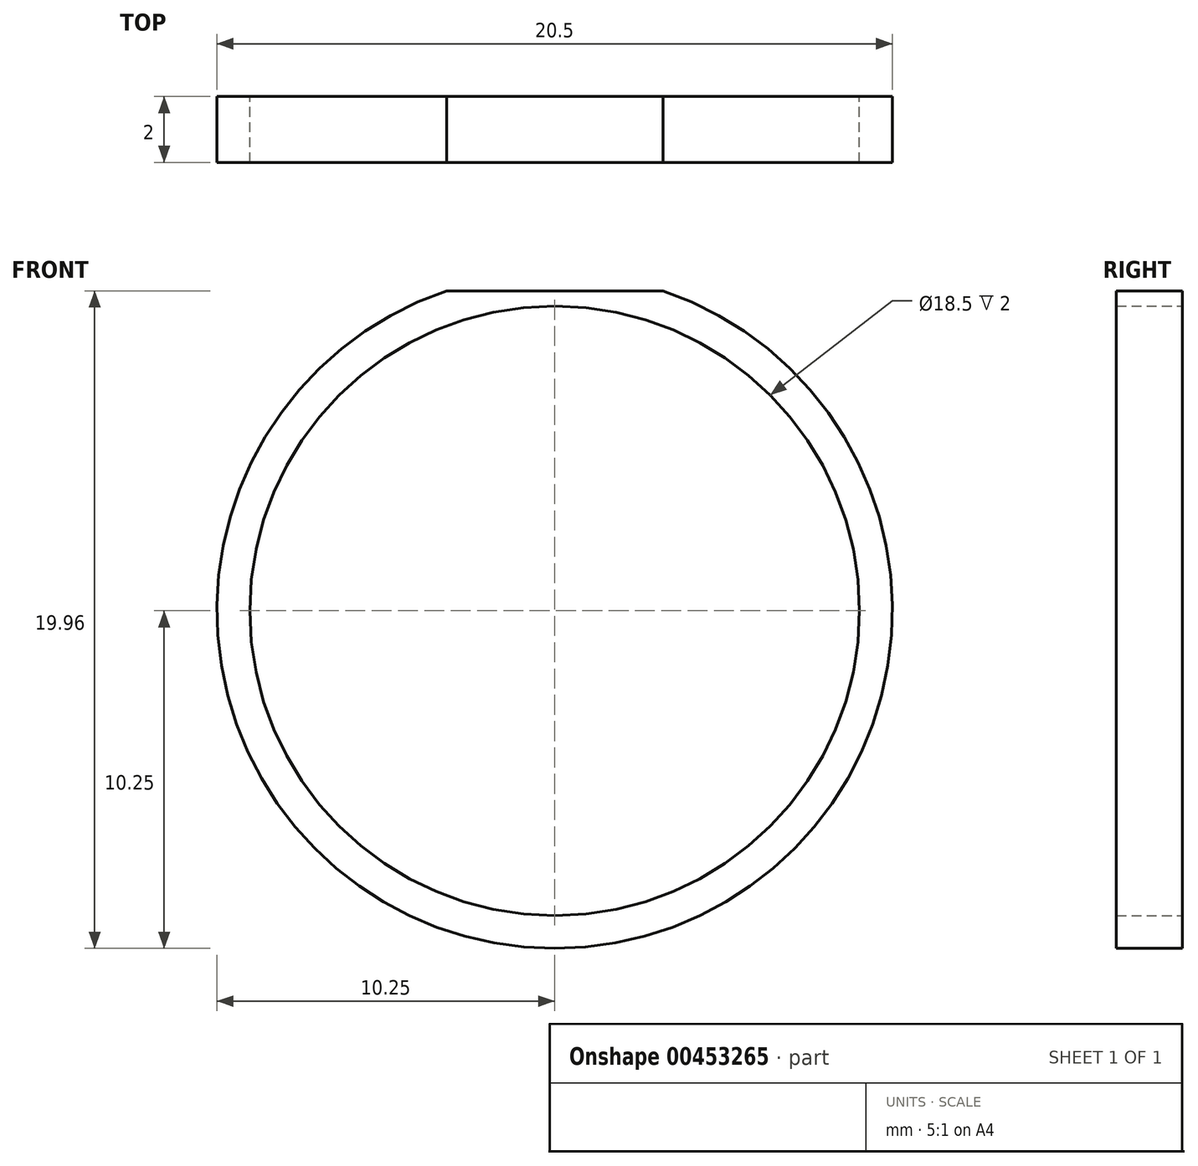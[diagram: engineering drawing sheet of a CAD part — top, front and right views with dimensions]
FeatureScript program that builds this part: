
annotation { "Feature Type Name" : "Feature", "Feature Type Description" : "" }
export const myFeature = defineFeature(function(context is Context, id is Id, definition is map)
    precondition{}
    {
        {
            var Q0;
            Q0=qCreatedBy(makeId("Front.planeOp"),FACE);
            var sketch = newSketch(context, id + "F0", { "sketchPlane" : qUnion([Q0])});
            skCircle(sketch, "E0", {"center": v(0, 0) * mm, "radius": 9.25 * mm});
            skArc(sketch, "E1", {"start": v(-3.28, 9.71) * mm, "mid": v(0, -10.25) * mm, "end": v(3.28, 9.71) * mm});
            skLineSegment(sketch, "E2", {"start": v(3.28, 9.71) * mm, "end": v(-3.28, 9.71) * mm});
            skSolve(sketch);
        }
        {
            var Q0;
            Q0=makeQuery(id+"F0.imprint","IMPRINT",FACE,{"disambiguationData":[TD([[makeQuery(id+"F0.imprint","IMPRINT",EDGE,{"derivedFrom":sQuery(id+"F0.wireOp",EDGE,"E0")}),-1.0]])]});
            extrude(context, id + "F1", {"entities" : qUnion([Q0]), "depth" : 2 * mm});
        }
    });
